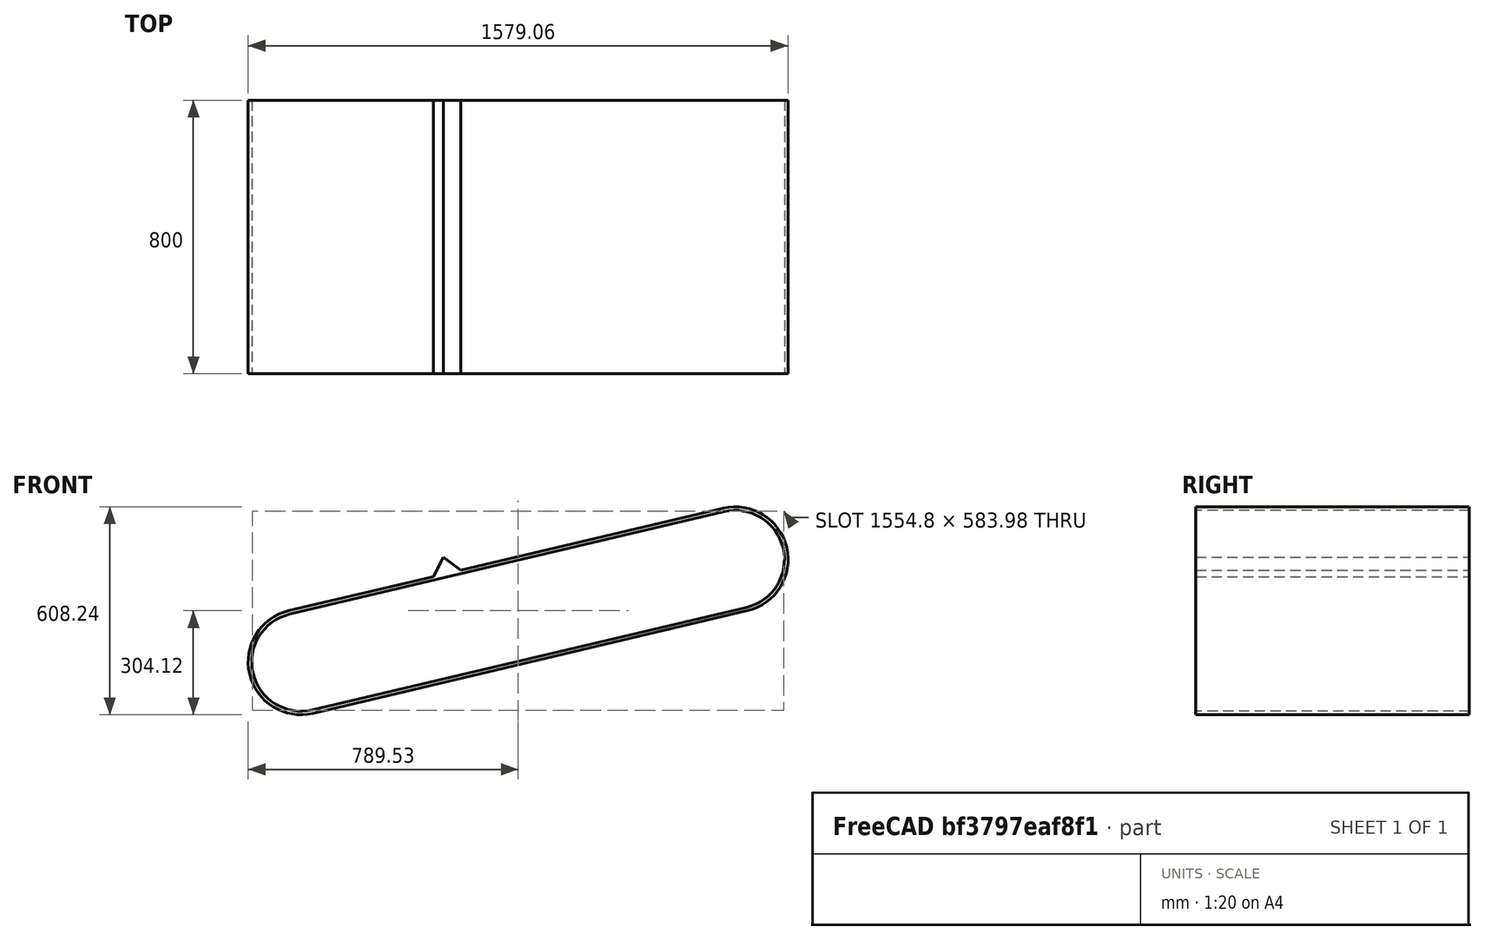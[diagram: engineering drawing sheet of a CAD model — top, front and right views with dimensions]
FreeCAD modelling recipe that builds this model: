
FCSTD DOCUMENT
Label: conveyor_belt
objects: Sketcher::SketchObject×1, PartDesign::Pad×1
note: 3 computed .brp shape members not serialized (recipe doc carries the construction recipe); baked Part::Feature solids carry a one-line shape summary decoded from their .brp

FEATURE [Sketcher::SketchObject] Sketch
  Placement = pos=(0,-400,0) rot=(-1,0,0;4.71239rad)
  sketch-geometry (11):
    g0: LineSegment StartX=-670.82 StartY=0 StartZ=0 EndX=-247.214 EndY=100 EndZ=0
    g1: LineSegment StartX=-600 StartY=-300 StartZ=0 EndX=670.82 EndY=7.25172e-07 EndZ=0
    g2: ArcOfCircle CenterX=635.41 CenterY=150 CenterZ=0 NormalX=0 NormalY=0 NormalZ=1 Radius=154.123 StartAngle=4.94421 EndAngle=8.08581
    g3: ArcOfCircle CenterX=-635.41 CenterY=-150 CenterZ=0 NormalX=0 NormalY=0 NormalZ=1 Radius=154.123 StartAngle=1.80262 EndAngle=4.94421
    g4: LineSegment StartX=-668.46 StartY=-10 StartZ=0 EndX=602.361 EndY=290 EndZ=0
    g5: LineSegment StartX=-602.361 StartY=-290 StartZ=0 EndX=668.46 EndY=10 EndZ=0
    g6: ArcOfCircle CenterX=-635.41 CenterY=-150 CenterZ=0 NormalX=0 NormalY=0 NormalZ=1 Radius=143.848 StartAngle=1.80262 EndAngle=4.94421
    g7: ArcOfCircle CenterX=635.41 CenterY=150 CenterZ=0 NormalX=0 NormalY=0 NormalZ=1 Radius=143.848 StartAngle=4.94421 EndAngle=8.08581
    g8: LineSegment StartX=-247.214 StartY=100 StartZ=0 EndX=-218.662 EndY=156.726 EndZ=0
    g9: LineSegment StartX=-218.662 StartY=156.726 StartZ=0 EndX=-167.756 EndY=118.757 EndZ=0
    g10: LineSegment StartX=-167.756 StartY=118.757 StartZ=0 EndX=600 EndY=300 EndZ=0
  constraints (34):
    c: Coincident(g2,g10)
    c: Coincident(g2,g1)
    c: Coincident(g3,g0)
    c: Coincident(g3,g1)
    c: Tangent(g3,g0)
    c: Tangent(g1,g3)
    c: Tangent(g2,g1)
    c: Tangent(g0,g2)
    c: Equal(g3,g2)
    c: DistanceY(g1) = -300
    c: DistanceY(g10) = 300
    c: DistanceX(g10) = 600
    c: DistanceX(g1) = -600
    c: DistanceY(g0) = 0
    c: Coincident(g6,g3)
    c: Coincident(g6,g4)
    c: Coincident(g6,g5)
    c: Coincident(g7,g2)
    c: Coincident(g7,g4)
    c: Coincident(g7,g5)
    c: Parallel(g5,g1)
    c: Parallel(g0,g4)
    c: Tangent(g4,g6)
    c: Tangent(g4,g7)
    c: Tangent(g6,g5)
    c: DistanceY(g4) = -10
    c: Coincident(g9,g8)
    c: Equal(g8,g9)
    c: Angle(g0,g8) = 0.872665
    c: Coincident(g0,g8)
    c: Coincident(g10,g9)
    c: Tangent(g0,g10)
    c: Distance(g8) = 63.5061
    c: DistanceY(g0) = 100
FEATURE [PartDesign::Pad] Pad
  Length = 800
  MirroredExtent = false
  Reversed = true
  Sketch = -> Sketch
